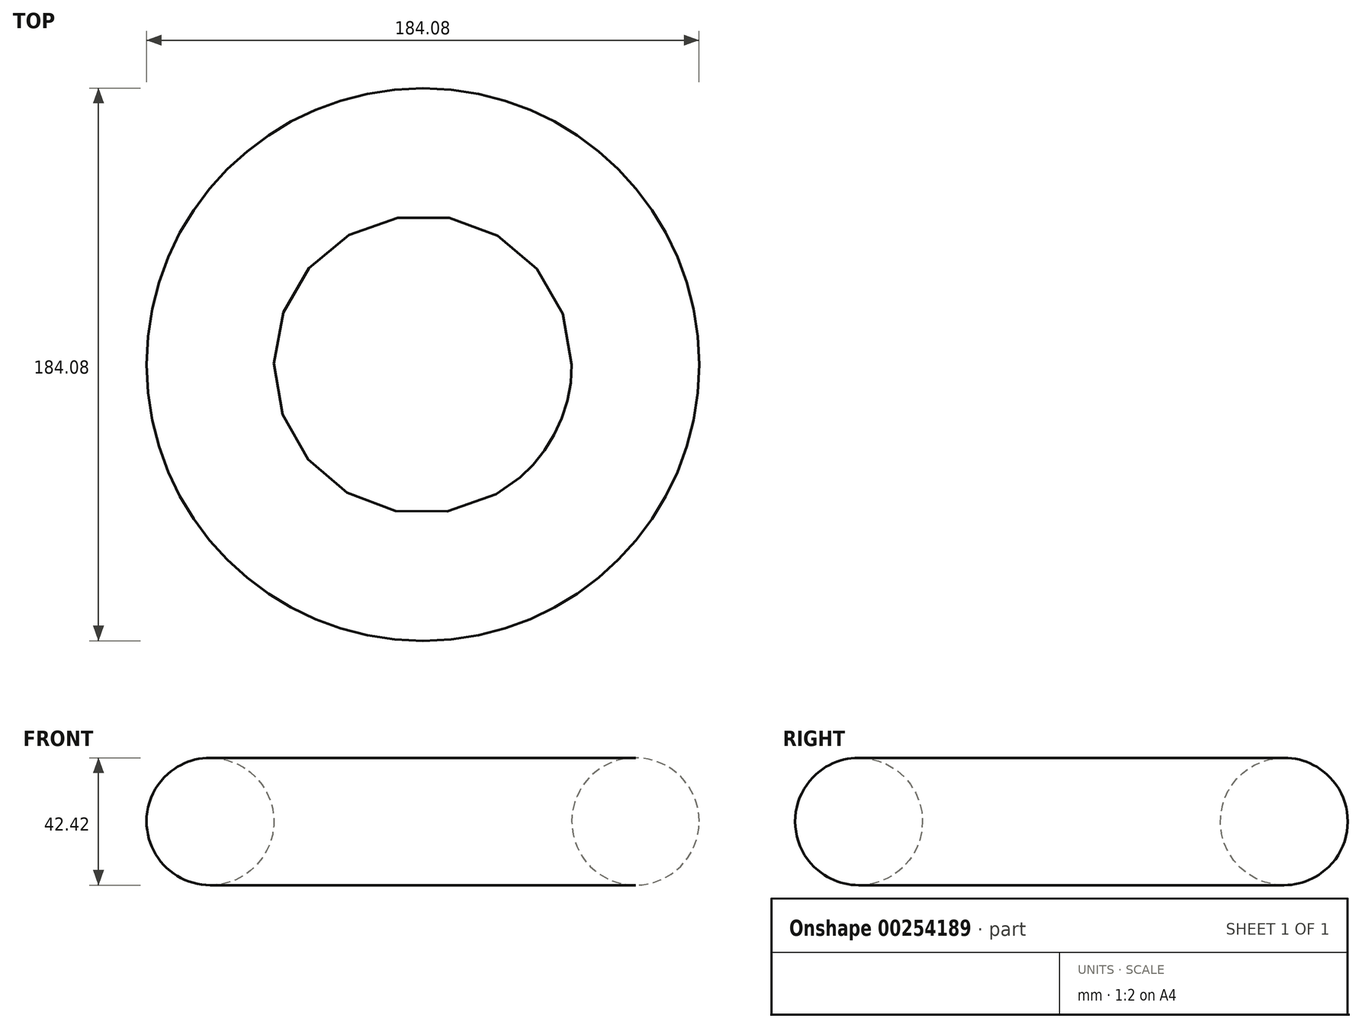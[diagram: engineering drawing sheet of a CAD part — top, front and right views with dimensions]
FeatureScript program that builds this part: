
annotation { "Feature Type Name" : "Feature", "Feature Type Description" : "" }
export const myFeature = defineFeature(function(context is Context, id is Id, definition is map)
    precondition{}
    {
        {
            var Q0;
            Q0=qCreatedBy(makeId("Front.planeOp"),FACE);
            var sketch = newSketch(context, id + "F0", { "sketchPlane" : qUnion([Q0])});
            skLineSegment(sketch, "E0", {"start": v(0, 77.42) * mm, "end": v(0, -77.66) * mm, "construction": true});
            skSolve(sketch);
        }
        {
            var Q0;
            Q0=qCreatedBy(makeId("Front.planeOp"),FACE);
            var sketch = newSketch(context, id + "F1", { "sketchPlane" : qUnion([Q0])});
            skCircle(sketch, "E1", {"center": v(-70.83, 13.18) * mm, "radius": 21.21 * mm});
            skSolve(sketch);
        }
        {
            var Q0;
            Q0=makeQuery(id+"F1.imprint","IMPRINT",FACE,{"disambiguationData":[TD([[makeQuery(id+"F1.imprint","IMPRINT",EDGE,{"derivedFrom":sQuery(id+"F1.wireOp",EDGE,"E1")}),1.0]])]});
            var Q1;
            Q1=sQuery(id+"F0.wireOp",EDGE,"E0");
            revolve(context, id + "F2", {"entities" : qUnion([Q0]), "axis" : qUnion([Q1]), "revolveType" : RevolveType.FULL});
        }
    });
